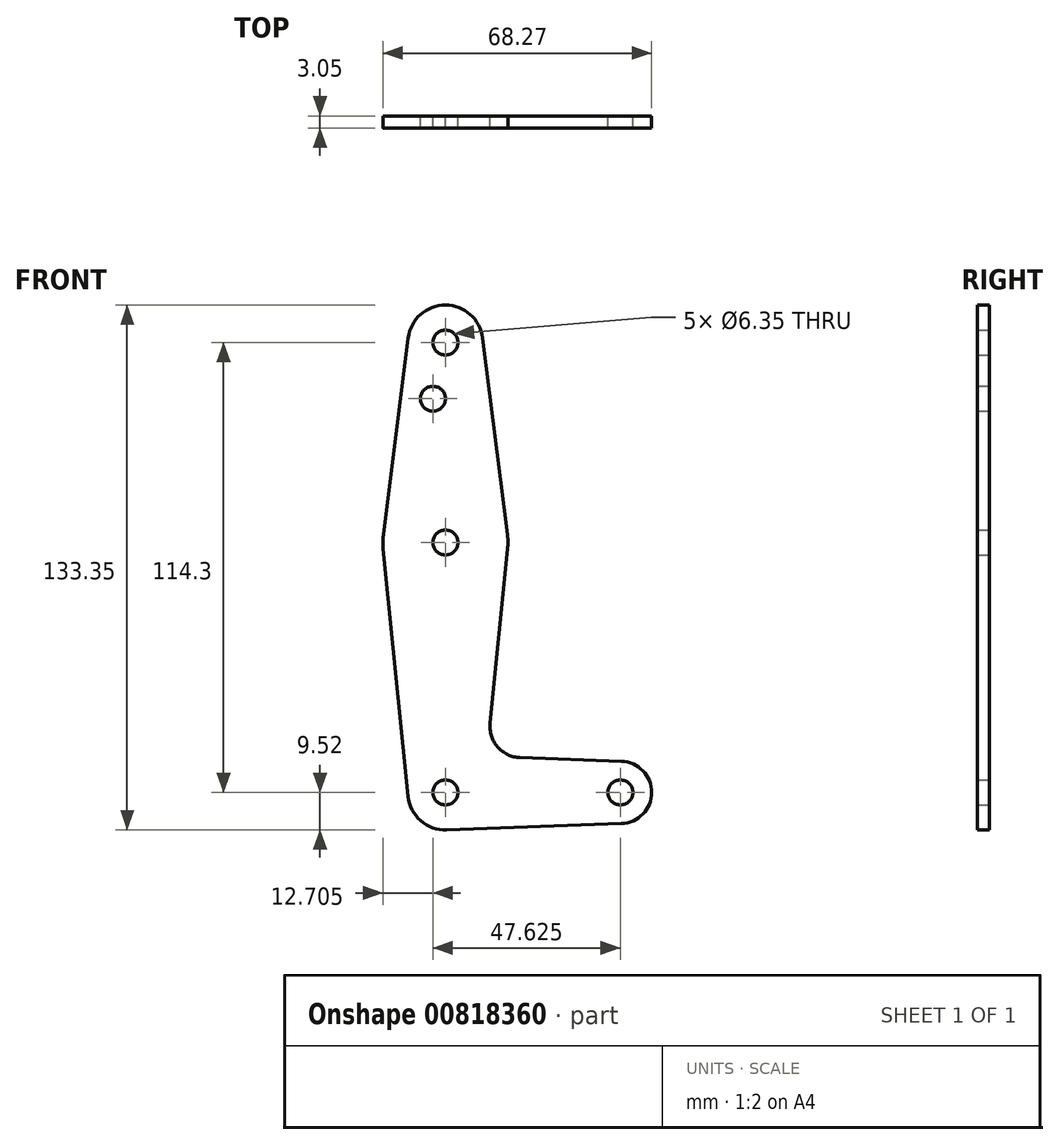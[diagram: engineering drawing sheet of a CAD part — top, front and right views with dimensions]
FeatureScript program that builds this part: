
annotation { "Feature Type Name" : "Feature", "Feature Type Description" : "" }
export const myFeature = defineFeature(function(context is Context, id is Id, definition is map)
    precondition{}
    {
        {
            var Q0;
            Q0=qCreatedBy(makeId("Front.planeOp"),FACE);
            var sketch = newSketch(context, id + "F0", { "sketchPlane" : qUnion([Q0])});
            skLineSegment(sketch, "E0", {"start": v(0, 114.3) * mm, "end": v(0, 0) * mm, "construction": true});
            skLineSegment(sketch, "E1", {"start": v(0, 0) * mm, "end": v(44.45, 0) * mm, "construction": true});
            skCircle(sketch, "E2", {"center": v(0, 0) * mm, "radius": 9.53 * mm});
            skCircle(sketch, "E3", {"center": v(0, 114.3) * mm, "radius": 9.53 * mm});
            skCircle(sketch, "E4", {"center": v(0, 63.5) * mm, "radius": 15.88 * mm});
            skCircle(sketch, "E5", {"center": v(44.45, 0) * mm, "radius": 7.94 * mm});
            skLineSegment(sketch, "E6", {"start": v(-9.45, 115.5) * mm, "end": v(-15.75, 65.48) * mm});
            skLineSegment(sketch, "E7", {"start": v(9.45, 115.5) * mm, "end": v(15.75, 65.48) * mm});
            skLineSegment(sketch, "E8", {"start": v(15.8, 61.91) * mm, "end": v(11.34, 17.6) * mm});
            skLineSegment(sketch, "E9", {"start": v(18.97, 8.85) * mm, "end": v(44.73, 7.93) * mm});
            skLineSegment(sketch, "E10", {"start": v(44.73, -7.93) * mm, "end": v(0, -9.53) * mm});
            skCircle(sketch, "E11", {"center": v(-3.18, 100.03) * mm, "radius": 3.18 * mm});
            skCircle(sketch, "E12", {"center": v(0, 63.5) * mm, "radius": 3.18 * mm});
            skCircle(sketch, "E13", {"center": v(0, 114.3) * mm, "radius": 3.18 * mm});
            skCircle(sketch, "E14", {"center": v(0, 0) * mm, "radius": 3.18 * mm});
            skCircle(sketch, "E15", {"center": v(44.45, 0) * mm, "radius": 3.18 * mm});
            skArc(sketch, "E16.filletArc", {"start": v(11.34, 17.6) * mm, "mid": v(13.26, 11.57) * mm, "end": v(18.97, 8.85) * mm});
            skLineSegment(sketch, "E17", {"start": v(-15.8, 61.91) * mm, "end": v(-9.48, -0.95) * mm});
            skSolve(sketch);
        }
        {
            var Q0;
            Q0 = qSketchRegion(id + "F0", true);
            extrude(context, id + "F1", {"entities" : qUnion([Q0]), "depth" : 3.05 * mm, "offsetDistance" : 25.4 * mm});
        }
    });
